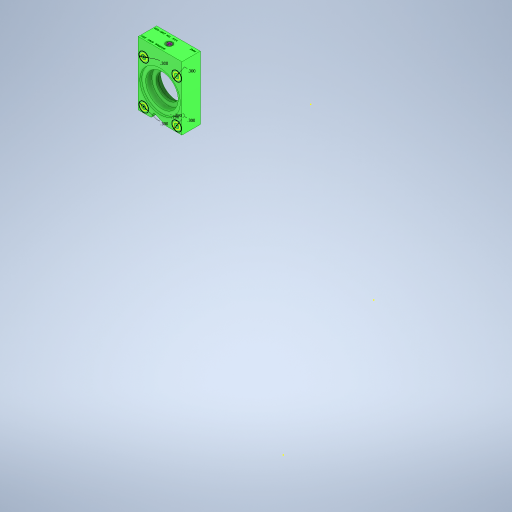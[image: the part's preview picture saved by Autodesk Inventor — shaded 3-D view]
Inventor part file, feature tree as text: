
AUTODESK INVENTOR PART (.ipt)
format: ipt  version: 2024.1 (Build 281209000, 209)  size: 721,408 bytes
history: native  units: in
note: dims shown in document units (in); Inventor stores cm internally (conversion verified against a paired STEP export)
features: hole x8, extrude x5, sketch x4, fillet x1
ambient origin geometry x8: Origin, YZ Plane, XZ Plane, XY Plane, X Axis, Y Axis, Z Axis, Center Point
bodies: Solid1 (feature_tree)
feature tree (18):
  extrude  "Extrusion1"  Depth=0.4in TaperAngle=0.0deg
  extrude  "Extrusion2"  Depth=0.375in
  extrude  "Extrusion3"  Depth=0.375in
  hole  "Hole1"  [1 undecoded]
  hole  "Hole2"  [1 undecoded]
  extrude  "Extrusion4"  Depth=0.375in
  hole  "Hole5"  [1 undecoded]
  hole  "Hole6"  [1 undecoded]
  fillet  "Fillet1"  Radius=1.0in
  sketch  "Sketch7"  dims[d13=0.06in d14=0.75in d15=0.507in d16=0.25in d17=0.5635in d18=1.0in d19=0.8108in d20=0.4583in d21=0.29in d22=0.04in d23=0.75in d24=0.507in d25=0.25in d26=0.5635in d27=1.0in d28=0.8108in d29=0.213in d30=0.75in d31=0.507in d32=0.25in d33=0.5635in d34=0.25in d35=0.0in d36=0.75in d38=135.0deg d39=0.4583in d40=112.5deg d41=0.25in d42=1.0in d43=0.0in d44=0.29in d45=0.196in d46=0.211in d47=0.25in d48=0.375in d49=0.25in d50=0.5635in d51=0.25in d52=0.0in d53=0.06in d54=0.75in d55=0.375in d56=0.25in d57=0.5635in d58=0.6in d59=0.8108in d60=0.0312in d61=0.13in d62=0.6in d63=0.375in d64=0.25in d65=0.5635in d66=0.484in d67=0.0in d68=0.5in d69=0.0in d70=0.3in d71=0.3in d72=0.3in d73=0.3in d74=0.136in d75=0.75in d76=0.375in d77=0.19in d78=0.5635in d79=1.0in d80=0.8108in]
  extrude  "Extrusion5"  Depth=0.375in
  hole  "Hole7"  [1 undecoded]
  hole  "Hole8"  [1 undecoded]
  hole  "Hole3"  [1 undecoded]
  hole  "Hole4"  [1 undecoded]
  sketch  "Sketch1"  dims[d0=0.5in d1=0.0in d2=0.4in d3=0.0in]
  sketch  "Sketch2"  dims[d4=0.6in d5=0.0in]
  sketch  "Sketch5"  dims[d6=0.211in d7=0.25in d8=0.507in d9=0.25in d10=0.5635in d11=0.25in d12=0.0in]
note: 8 required parameter values undecoded (feature->parameter linkage not recoverable at this tier; creation-order binding heuristic only, values carry confidence <= 0.55)
